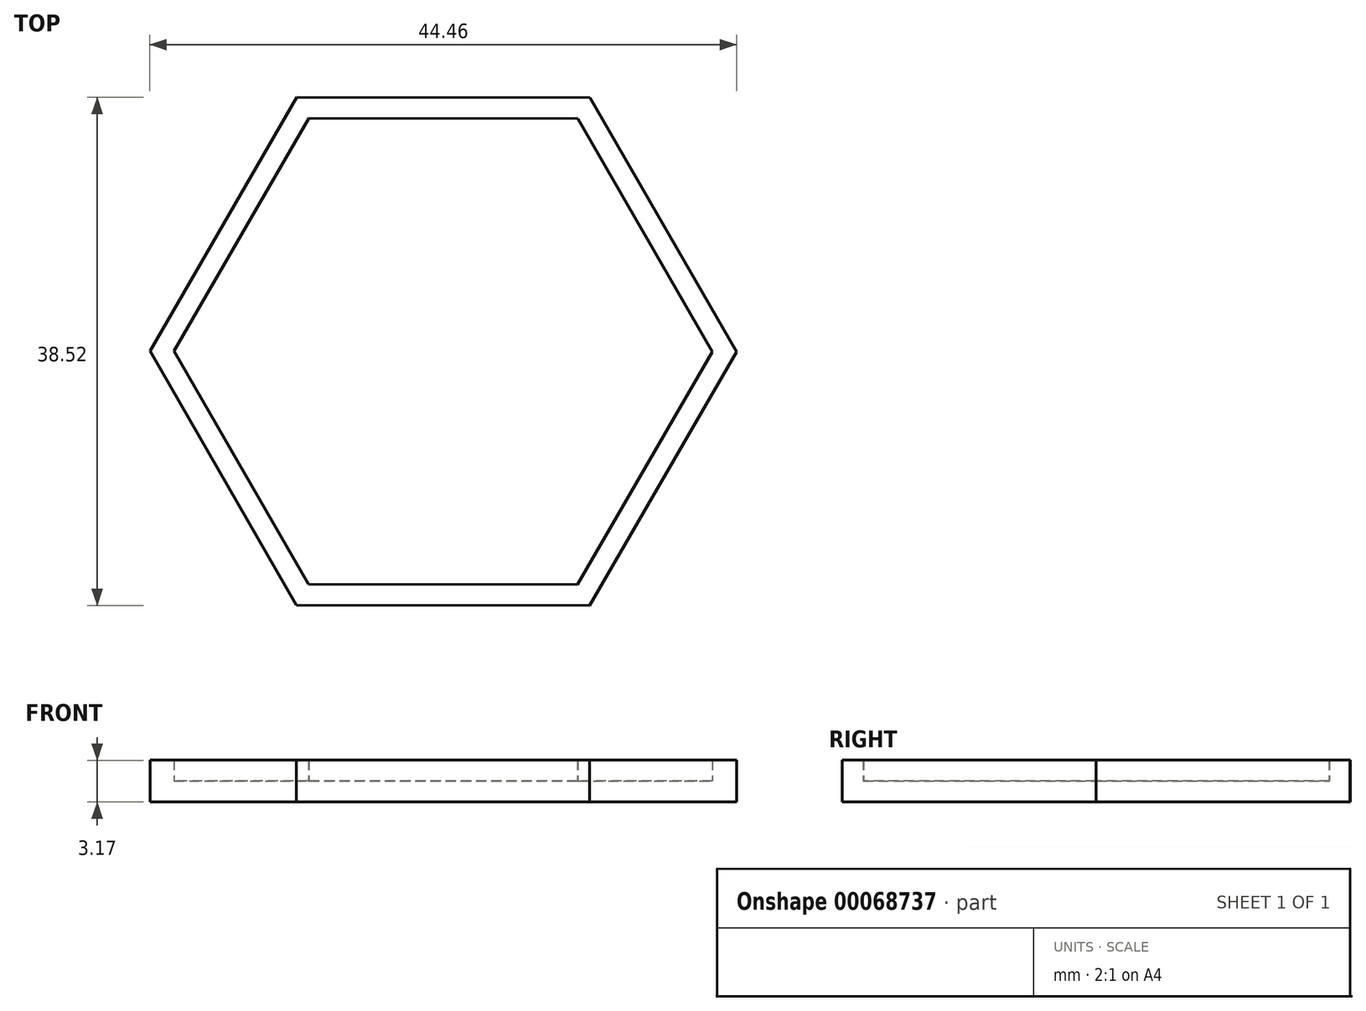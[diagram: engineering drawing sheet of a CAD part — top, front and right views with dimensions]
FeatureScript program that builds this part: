
annotation { "Feature Type Name" : "Feature", "Feature Type Description" : "" }
export const myFeature = defineFeature(function(context is Context, id is Id, definition is map)
    precondition{}
    {
        {
            var Q0;
            Q0=qCreatedBy(makeId("Top.planeOp"),FACE);
            var sketch = newSketch(context, id + "F0", { "sketchPlane" : qUnion([Q0])});
            skCircle(sketch, "E0.cCircle", {"center": v(0, 0) * mm, "radius": 19.25 * mm, "construction": true});
            skLineSegment(sketch, "E0.0", {"start": v(11.14, 19.23) * mm, "end": v(22.22, -0.03) * mm});
            skLineSegment(sketch, "E0.1", {"start": v(22.22, -0.03) * mm, "end": v(11.09, -19.26) * mm});
            skLineSegment(sketch, "E0.2", {"start": v(11.09, -19.26) * mm, "end": v(-11.14, -19.23) * mm});
            skLineSegment(sketch, "E0.3", {"start": v(-11.14, -19.23) * mm, "end": v(-22.22, 0.03) * mm});
            skLineSegment(sketch, "E0.4", {"start": v(-22.23, 0.03) * mm, "end": v(-11.09, 19.26) * mm});
            skLineSegment(sketch, "E0.5", {"start": v(-11.09, 19.26) * mm, "end": v(11.14, 19.23) * mm});
            skPoint(sketch, "E0.0.midPoint", {"position": v(16.68, 9.6) * mm});
            skSolve(sketch);
        }
        {
            var Q0;
            Q0 = qSketchRegion(id + "F0", true);
            extrude(context, id + "F1", {"entities" : qUnion([Q0]), "depth" : 3.17 * mm});
        }
        {
            var Q0;
            Q0=makeQuery(id+"F1.opExtrude","CAP_FACE",FACE,{"disambiguationData":[OSD([sQuery(id+"F0.wireOp",EDGE,"E0.0"),sQuery(id+"F0.wireOp",EDGE,"E0.1"),sQuery(id+"F0.wireOp",EDGE,"E0.2"),sQuery(id+"F0.wireOp",EDGE,"E0.3"),sQuery(id+"F0.wireOp",EDGE,"E0.4"),sQuery(id+"F0.wireOp",EDGE,"E0.5")])],"isStart":false});
            shell(context, id + "F2", {"entities" : qUnion([Q0]), "thickness" : 1.59 * mm});
        }
    });
